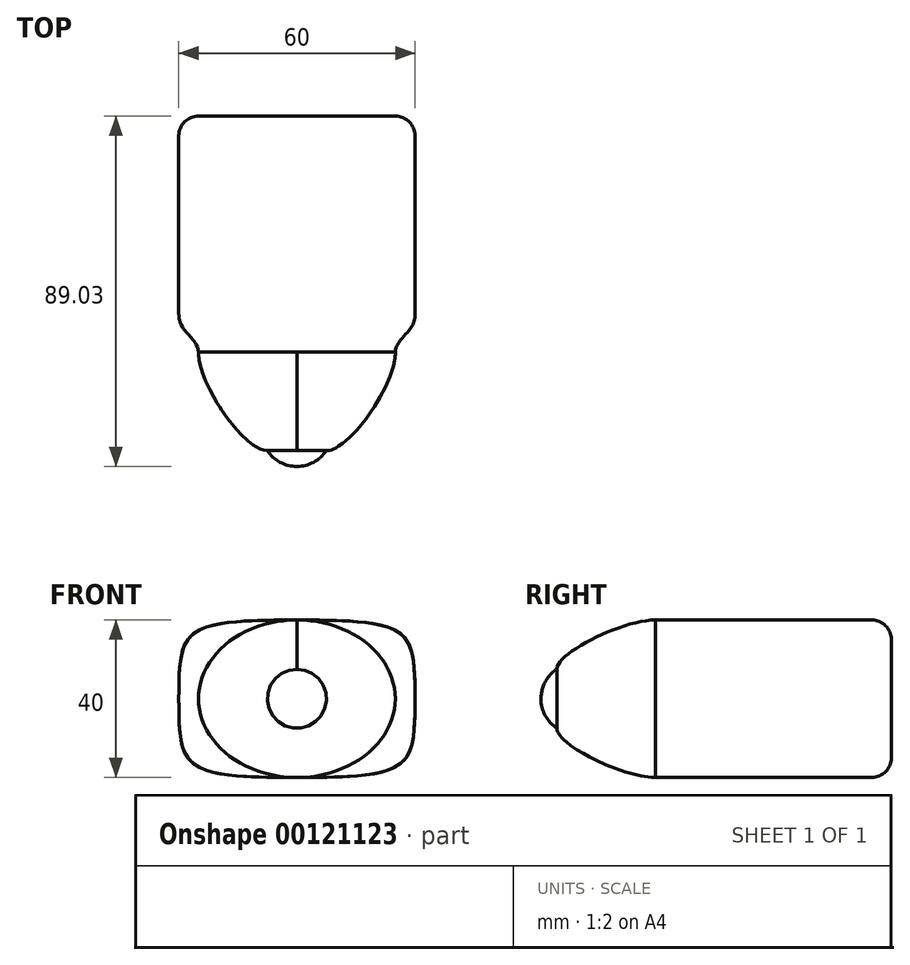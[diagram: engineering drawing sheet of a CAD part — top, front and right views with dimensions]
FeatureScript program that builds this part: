
annotation { "Feature Type Name" : "Feature", "Feature Type Description" : "" }
export const myFeature = defineFeature(function(context is Context, id is Id, definition is map)
    precondition{}
    {
        {
            var Q0;
            Q0=qCreatedBy(makeId("Right.planeOp"),FACE);
            var sketch = newSketch(context, id + "F0", { "sketchPlane" : qUnion([Q0])});
            skLineSegment(sketch, "E0", {"start": v(0, 0) * mm, "end": v(-25, 0) * mm});
            skLineSegment(sketch, "E1", {"start": v(-25, 7.5) * mm, "end": v(-25, -7.5) * mm});
            skArc(sketch, "E2", {"start": v(-25, 7.5) * mm, "mid": v(-29.03, 0) * mm, "end": v(-25, -7.5) * mm});
            skLineSegment(sketch, "E3", {"start": v(-25, 0) * mm, "end": v(-29.03, 0) * mm});
            skLineSegment(sketch, "E4", {"start": v(0, 20) * mm, "end": v(0, -20) * mm});
            skLineSegment(sketch, "E5", {"start": v(0, 0) * mm, "end": v(65.71, 0) * mm});
            skLineSegment(sketch, "E6", {"start": v(0, 20) * mm, "end": v(60, 20) * mm});
            skLineSegment(sketch, "E7", {"start": v(30, 20) * mm, "end": v(30, -20) * mm});
            skLineSegment(sketch, "E8", {"start": v(0, -20) * mm, "end": v(61.05, -20) * mm});
            skFitSpline(sketch, "E9", {"points": [v(30, 20) * mm, v(0, 0) * mm], "startDerivative": vector(-87.7, 0) * mm, "endDerivative": vector(0, -53.87) * mm});
            skFitSpline(sketch, "E10.MirrorCS", {"points": [v(30, 20) * mm, v(60, 0) * mm], "startDerivative": vector(87.7, 0) * mm, "endDerivative": vector(0, -53.87) * mm});
            skFitSpline(sketch, "E11.MirrorCS", {"points": [v(30, -20) * mm, v(0, 0) * mm], "startDerivative": vector(-87.7, 0) * mm, "endDerivative": vector(0, 53.87) * mm});
            skFitSpline(sketch, "E12.MirrorCS", {"points": [v(30, -20) * mm, v(60, 0) * mm], "startDerivative": vector(87.7, 0) * mm, "endDerivative": vector(0, 53.87) * mm});
            skFitSpline(sketch, "E13", {"points": [v(-25, 7.5) * mm, v(0, 20) * mm], "startDerivative": vector(27.72, 6.25) * mm, "endDerivative": vector(27.58, 0) * mm});
            skFitSpline(sketch, "E14.MirrorCS", {"points": [v(-25, -7.5) * mm, v(0, -20) * mm], "startDerivative": vector(27.72, -6.25) * mm, "endDerivative": vector(27.58, 0) * mm});
            skLineSegment(sketch, "E15", {"start": v(0, 20) * mm, "end": v(30, 20) * mm});
            skLineSegment(sketch, "E16", {"start": v(0, -20) * mm, "end": v(30, -20) * mm});
            skSolve(sketch);
        }
        {
            var Q0;
            {var subQ0=sQuery(id+"F0.wireOp",EDGE,"E3");Q0=makeQuery(id+"F0.imprint","IMPRINT",FACE,{"disambiguationData":[TD([[makeQuery(id+"F0.imprint","IMPRINT",EDGE,{"derivedFrom":subQ0}),-1.0]])]});}
            var Q1;
            Q1=sQuery(id+"F0.wireOp",EDGE,"E3");
            revolve(context, id + "F1", {"entities" : qUnion([Q0]), "axis" : qUnion([Q1]), "revolveType" : RevolveType.FULL});
        }
        {
            var Q0;
            Q0=qCreatedBy(makeId("Front.planeOp"),FACE);
            var sketch = newSketch(context, id + "F2", { "sketchPlane" : qUnion([Q0])});
            skEllipse(sketch, "E17", {"center": v(0, 0) * mm, "majorRadius": 25 * mm, "minorRadius": 20 * mm, "majorAxis": v(-1, 0)});
            skSolve(sketch);
        }
        {
            var Q0;
            {var subQ0=sQuery(id+"F0.wireOp",EDGE,"E10.MirrorCS");Q0=makeQuery(id+"F0.imprint","IMPRINT",FACE,{"disambiguationData":[TD([[makeQuery(id+"F0.imprint","IMPRINT",EDGE,{"derivedFrom":subQ0}),-1.0]])]});}
            var Q1;
            {var subQ0=sQuery(id+"F0.wireOp",EDGE,"E12.MirrorCS");Q1=makeQuery(id+"F0.imprint","IMPRINT",FACE,{"disambiguationData":[TD([[makeQuery(id+"F0.imprint","IMPRINT",EDGE,{"derivedFrom":subQ0}),1.0]])]});}
            var Q2;
            Q2=sQuery(id+"F0.wireOp",EDGE,"E7");
            revolve(context, id + "F3", {"entities" : qUnion([Q0, Q1]), "axis" : qUnion([Q2]), "revolveType" : RevolveType.SYMMETRIC, "angle" : 180 * degree});
        }
        {
            var Q1;
            Q1=makeQuery(id+"F1.opRevolve","SWEPT_FACE",FACE,{"disambiguationData":[OSD([sQuery(id+"F0.wireOp",EDGE,"E1")])]});
            var Q2;
            Q2=makeQuery(id+"F2.imprint","IMPRINT",FACE,{"disambiguationData":[TD([[makeQuery(id+"F2.imprint","IMPRINT",EDGE,{"derivedFrom":sQuery(id+"F2.wireOp",EDGE,"E17")}),1.0]])]});
            loft(context, id + "F4", {"operationType" : NewBodyOperationType.ADD, "startCondition" : LoftEndDerivativeType.TANGENT_TO_PROFILE, "startMagnitude" : 1, "endCondition" : LoftEndDerivativeType.NORMAL_TO_PROFILE, "endMagnitude" : 1, "sheetProfilesArray" : [{ "sheetProfileEntities" : qUnion([Q1]) }, { "sheetProfileEntities" : qUnion([Q2]) }]});
        }
        {
            var Q0;
            Q0=makeQuery(id+"F3.opRevolve","CAP_FACE",FACE,{"disambiguationData":[OSD([sQuery(id+"F0.wireOp",EDGE,"E7"),sQuery(id+"F0.wireOp",EDGE,"E10.MirrorCS"),sQuery(id+"F0.wireOp",EDGE,"E12.MirrorCS")])],"isStart":false});
            var sketch = newSketch(context, id + "F5", { "sketchPlane" : qUnion([Q0])});
            skSolve(sketch);
        }
        {
            var Q0;
            {var subQ0=sQuery(id+"F0.wireOp",EDGE,"E10.MirrorCS");Q0=makeQuery(id+"F5.imprint","IMPRINT",FACE,{"disambiguationData":[TD([[makeQuery(id+"F5.imprint","IMPRINT",EDGE,{"derivedFrom":makeQuery(id+"F3.opRevolve","CAP_EDGE",EDGE,{"disambiguationData":[OSD([subQ0])],"isStart":true})}),1.0]])]});}
            extrude(context, id + "F6", {"entities" : qUnion([Q0]), "operationType" : NewBodyOperationType.ADD, "oppositeDirection" : true, "depth" : 30 * mm});
        }
        {
            var Q0;
            {var subQ0=sQuery(id+"F0.wireOp",EDGE,"E10.MirrorCS");Q0=makeQuery(id+"F6.opExtrude","CAP_EDGE",EDGE,{"disambiguationData":[OSD([subQ0]),TDD([makeQuery(id+"F5.imprint","IMPRINT",EDGE,{"derivedFrom":makeQuery(id+"F3.opRevolve","CAP_EDGE",EDGE,{"disambiguationData":[OSD([subQ0])],"isStart":false})})])],"isStart":false});}
            fillet(context, id + "F7", {"entities" : qUnion([Q0]), "radius" : 5 * mm, "tangentPropagation" : true, "allowEdgeOverflow" : false});
        }
        {
            var Q0;
            Q0=makeQuery(id+"F3.opRevolve","CAP_FACE",FACE,{"disambiguationData":[OSD([sQuery(id+"F0.wireOp",EDGE,"E7"),sQuery(id+"F0.wireOp",EDGE,"E10.MirrorCS"),sQuery(id+"F0.wireOp",EDGE,"E12.MirrorCS")])],"isStart":false});
            extrude(context, id + "F8", {"entities" : qUnion([Q0]), "operationType" : NewBodyOperationType.ADD, "depth" : 20 * mm});
        }
        {
            var Q1;
            Q1=makeQuery(id+"F2.imprint","IMPRINT",FACE,{"disambiguationData":[TD([[makeQuery(id+"F2.imprint","IMPRINT",EDGE,{"derivedFrom":sQuery(id+"F2.wireOp",EDGE,"E17")}),1.0]])]});
            var Q2;
            Q2=makeQuery(id+"F8.opExtrude","CAP_FACE",FACE,{"disambiguationData":[OSD([sQuery(id+"F0.wireOp",EDGE,"E7"),sQuery(id+"F0.wireOp",EDGE,"E10.MirrorCS"),sQuery(id+"F0.wireOp",EDGE,"E12.MirrorCS")])],"isStart":false});
            loft(context, id + "F9", {"operationType" : NewBodyOperationType.ADD, "startCondition" : LoftEndDerivativeType.NORMAL_TO_PROFILE, "startMagnitude" : 1, "endCondition" : LoftEndDerivativeType.MATCH_CURVATURE, "endMagnitude" : 1, "sheetProfilesArray" : [{ "sheetProfileEntities" : qUnion([Q1]) }, { "sheetProfileEntities" : qUnion([Q2]) }]});
        }
    });
